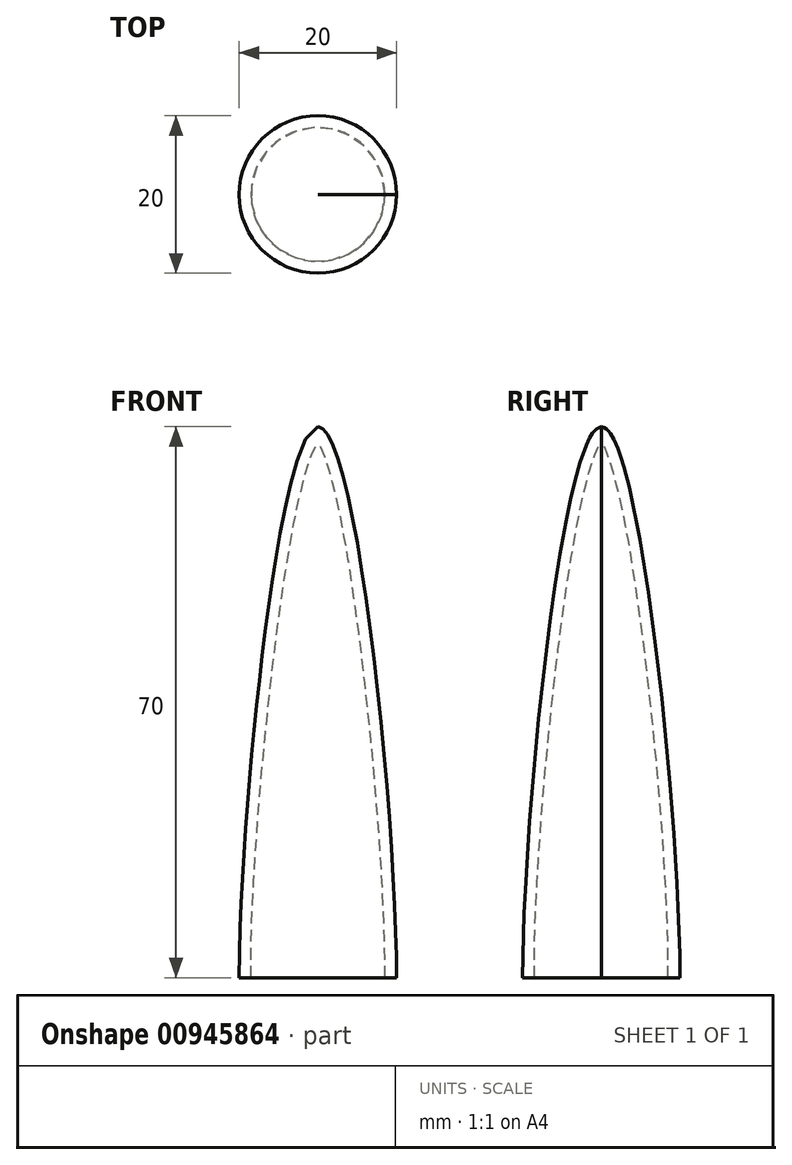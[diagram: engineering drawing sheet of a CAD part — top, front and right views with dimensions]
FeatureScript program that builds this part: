
annotation { "Feature Type Name" : "Feature", "Feature Type Description" : "" }
export const myFeature = defineFeature(function(context is Context, id is Id, definition is map)
    precondition{}
    {
        {
            var Q0;
            Q0=qCreatedBy(makeId("Front.planeOp"),FACE);
            var sketch = newSketch(context, id + "F0", { "sketchPlane" : qUnion([Q0])});
            skLineSegment(sketch, "E0", {"start": v(0, 0) * mm, "end": v(0, 70) * mm});
            skLineSegment(sketch, "E1", {"start": v(0, 0) * mm, "end": v(10, 0) * mm});
            skFitSpline(sketch, "E2", {"points": [v(10, 0) * mm, v(0, 70) * mm], "startDerivative": vector(0, 60) * mm, "endDerivative": vector(-15, 0) * mm});
            skLineSegment(sketch, "E3", {"start": v(10, 0) * mm, "end": v(10, 77.29) * mm, "construction": true});
            skLineSegment(sketch, "E4", {"start": v(0, 70) * mm, "end": v(39.59, 70) * mm, "construction": true});
            skFitSpline(sketch, "E5.0", {"points": [v(8.5, 0) * mm, v(8.5, 2.4) * mm, v(8.35, 8.1) * mm, v(7.75, 18.49) * mm, v(6.96, 27.92) * mm, v(6.2, 35.5) * mm, v(5.55, 41.1) * mm, v(4.85, 46.49) * mm, v(4.1, 51.58) * mm, v(3.32, 56.24) * mm, v(2.64, 59.68) * mm, v(2.08, 62.11) * mm, v(1.66, 63.76) * mm, v(1.24, 65.2) * mm, v(0.82, 66.44) * mm, v(0.48, 67.27) * mm, v(0.22, 67.8) * mm, v(0.04, 68.12) * mm, v(-0.1, 68.32) * mm, v(-0.19, 68.44) * mm, v(-0.25, 68.5) * mm, v(-0.28, 68.55) * mm, v(-0.3, 68.57) * mm, v(-0.31, 68.58) * mm, v(-0.32, 68.58) * mm, v(-0.32, 68.58) * mm, v(-0.32, 68.58) * mm, v(-0.32, 68.58) * mm, v(-0.32, 68.58) * mm, v(-0.33, 68.59) * mm, v(-0.34, 68.6) * mm, v(-0.36, 68.6) * mm, v(-0.38, 68.62) * mm, v(-0.42, 68.65) * mm, v(-0.45, 68.67) * mm, v(-0.47, 68.69) * mm]});
            skLineSegment(sketch, "E6", {"start": v(0, 58.17) * mm, "end": v(2.93, 58.17) * mm});
            skSolve(sketch);
        }
        {
            var Q0;
            {var subQ0=sQuery(id+"F0.wireOp",EDGE,"E2");Q0=makeQuery(id+"F0.imprint","IMPRINT",FACE,{"disambiguationData":[TD([[makeQuery(id+"F0.imprint","IMPRINT",EDGE,{"derivedFrom":subQ0}),1.0]])]});}
            var Q1;
            {var subQ3=sQuery(id+"F0.wireOp",EDGE,"E6");Q1=makeQuery(id+"F0.imprint","IMPRINT",FACE,{"disambiguationData":[TD([[makeQuery(id+"F0.imprint","IMPRINT",EDGE,{"derivedFrom":subQ3}),1.0]])]});}
            var Q2;
            Q2=sQuery(id+"F0.wireOp",EDGE,"E0");
            revolve(context, id + "F1", {"surfaceOperationType" : NewSurfaceOperationType.NEW, "entities" : qUnion([Q0, Q1]), "axis" : qUnion([Q2]), "revolveType" : RevolveType.FULL});
        }
    });
